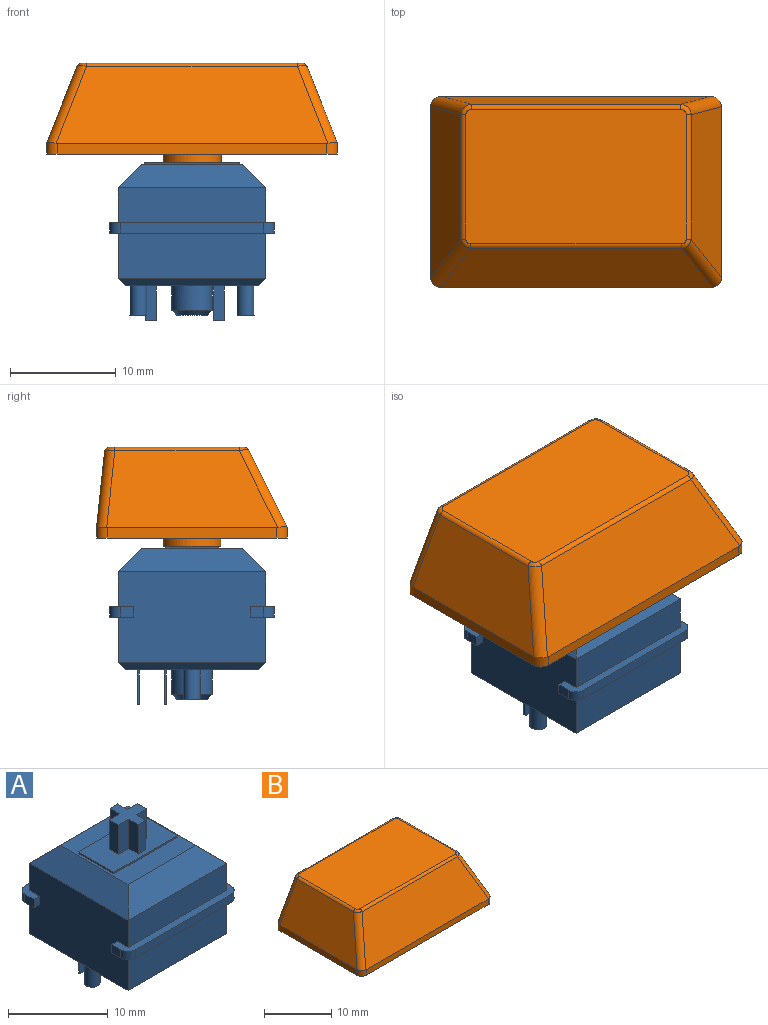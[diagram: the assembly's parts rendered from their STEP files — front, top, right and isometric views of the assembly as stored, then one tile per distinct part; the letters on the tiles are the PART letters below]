
ASSEMBLY  parts=2 mates=1
PART A: 69 faces, bbox 15.6x15.6x18.6 mm
  f0: plane 15.6x2.3mm, normal (0,0,-1), area 14.4mm2, adj f2,f3,f28,f30,f35,f60,f62,f63
  f1: plane 15.6x2.3mm, normal (0,0,-1), area 14.4mm2, adj f28,f30,f33,f34,f36,f59,f61,f64
  f2: plane 1.3x1mm, normal (1,0,0), area 1.3mm2, adj f0,f32,f62,f66
  f3: plane 1.3x1mm, normal (-1,0,0), area 1.3mm2, adj f0,f32,f63,f68
  f4: plane 15.6x2.3mm, normal (0,0,1), area 14.4mm2, adj f28,f30,f31,f33,f34,f36,f61,f64
  f5: plane 14x2.2mm, normal (-0.71,0,0.71), area 36.7mm2, adj f6,f7,f26,f30
  f6: plane 14x2.2mm, normal (0,-0.71,0.71), area 36.7mm2, adj f5,f7,f27,f31
  f7: plane 9.6x9.6mm, normal (0,0,1), area 47.2mm2, adj f5,f6,f8,f9,f10,f11,f26,f27
  f8: plane 5x0.2mm, normal (1,0,0), area 1mm2, adj f7,f9,f11,f12
  f9: plane 9x0.2mm, normal (0,1,0), area 1.8mm2, adj f7,f8,f10,f12
  f10: plane 5x0.2mm, normal (-1,0,0), area 1mm2, adj f7,f9,f11,f12
  f11: plane 9x0.2mm, normal (0,-1,0), area 1.8mm2, adj f7,f8,f10,f12
  f12: plane 9x5mm, normal (0,0,1), area 36.9mm2, adj f8,f9,f10,f11,f13,f14,f15,f16
  f13: plane 3.6x1.35mm, normal (1,0,0), area 4.9mm2, adj f12,f14,f24,f25
  f14: plane 3.6x1.08mm, normal (0,1,0), area 3.9mm2, adj f12,f13,f15,f25
  f15: plane 3.6x1.35mm, normal (-1,0,0), area 4.9mm2, adj f12,f14,f16,f25
  f16: plane 3.6x1.46mm, normal (0,1,0), area 5.3mm2, adj f12,f15,f17,f25
  f17: plane 3.6x1.3mm, normal (-1,0,0), area 4.7mm2, adj f12,f16,f18,f25
  f18: plane 3.6x1.46mm, normal (0,-1,0), area 5.3mm2, adj f12,f17,f19,f25
  f19: plane 3.6x1.35mm, normal (-1,0,0), area 4.9mm2, adj f12,f18,f20,f25
  f20: plane 3.6x1.08mm, normal (0,-1,0), area 3.9mm2, adj f12,f19,f21,f25
  f21: plane 3.6x1.35mm, normal (1,0,0), area 4.9mm2, adj f12,f20,f22,f25
  f22: plane 3.6x1.46mm, normal (0,-1,0), area 5.3mm2, adj f12,f21,f23,f25
  f23: plane 3.6x1.3mm, normal (1,0,0), area 4.7mm2, adj f12,f22,f24,f25
  f24: plane 3.6x1.46mm, normal (0,1,0), area 5.3mm2, adj f12,f13,f23,f25
  f25: plane 4x4mm, normal (0,0,1), area 8.1mm2, adj f13,f14,f15,f16,f17,f18,f19,f20
  f26: plane 14x2.2mm, normal (0,0.71,0.71), area 36.7mm2, adj f5,f7,f27,f29
  f27: plane 14x2.2mm, normal (0.71,0,0.71), area 36.7mm2, adj f6,f7,f26,f28
  f28: plane 14x8.6mm, normal (1,0,0), area 117.4mm2, adj f0,f1,f4,f27,f29,f31,f32,f55
  f29: plane 14x3.3mm, normal (0,1,0), area 46.2mm2, adj f26,f28,f30,f32
  f30: plane 14x8.6mm, normal (-1,0,0), area 117.4mm2, adj f0,f1,f4,f5,f29,f31,f32,f57
  f31: plane 14x3.3mm, normal (0,-1,0), area 46.2mm2, adj f4,f6,f28,f30
  f32: plane 15.6x2.3mm, normal (0,0,1), area 14.4mm2, adj f2,f3,f28,f29,f30,f35,f62,f63
  f33: plane 13.6x1mm, normal (0,-1,0), area 13.6mm2, adj f1,f4,f61,f64
  f34: plane 1.3x1mm, normal (1,0,0), area 1.3mm2, adj f1,f4,f61,f65
  f35: plane 13.6x1mm, normal (0,1,0), area 13.6mm2, adj f0,f32,f62,f63
  f36: plane 1.3x1mm, normal (-1,0,0), area 1.3mm2, adj f1,f4,f64,f67
  f37: plane 2.85x2.85mm, normal (0,0,-1), area 6.4mm2, adj f38
  f38: cone r=1.43mm half-angle=45deg, axis (0,0,1), area 7.4mm2, adj f37,f43
  f39: plane 1x0.2mm, normal (0,0,-1), area 0.2mm2, adj f44,f45,f46,f47
  f40: plane 1x0.2mm, normal (0,0,-1), area 0.2mm2, adj f48,f49,f50,f51
  f41: plane 1.6x1.6mm, normal (0,0,-1), area 2mm2, adj f52
  f42: plane 1.6x1.6mm, normal (0,0,-1), area 2mm2, adj f53
  f43: cylinder r=1.93mm len=3.85mm, axis (0,0,1), area 27.8mm2, adj f38,f54
  f44: plane 3.3x0.2mm, normal (-1,0,0), area 0.7mm2, adj f39,f45,f47,f54
  f45: plane 3.3x1mm, normal (0,1,0), area 3.3mm2, adj f39,f44,f46,f54
  f46: plane 3.3x0.2mm, normal (1,0,0), area 0.7mm2, adj f39,f45,f47,f54
  f47: plane 3.3x1mm, normal (0,-1,0), area 3.3mm2, adj f39,f44,f46,f54
  f48: plane 3.3x0.2mm, normal (-1,0,0), area 0.7mm2, adj f40,f49,f51,f54
  f49: plane 3.3x1mm, normal (0,1,0), area 3.3mm2, adj f40,f48,f50,f54
  f50: plane 3.3x0.2mm, normal (1,0,0), area 0.7mm2, adj f40,f49,f51,f54
  f51: plane 3.3x1mm, normal (0,-1,0), area 3.3mm2, adj f40,f48,f50,f54
  f52: cylinder r=0.8mm len=2.8mm, axis (0,0,1), area 14.1mm2, adj f41,f54
  f53: cylinder r=0.8mm len=2.8mm, axis (0,0,1), area 14.1mm2, adj f42,f54
  f54: plane 12.6x12.6mm, normal (0,0,-1), area 142.7mm2, adj f43,f44,f45,f46,f47,f48,f49,f50
  f55: plane 14x0.7mm, normal (0.71,0,-0.71), area 13.2mm2, adj f28,f54,f56,f58
  f56: plane 14x0.7mm, normal (0,0.71,-0.71), area 13.2mm2, adj f54,f55,f57,f60
  f57: plane 14x0.7mm, normal (-0.71,0,-0.71), area 13.2mm2, adj f30,f54,f56,f58
  f58: plane 14x0.7mm, normal (0,-0.71,-0.71), area 13.2mm2, adj f54,f55,f57,f59
  f59: plane 14x4.3mm, normal (0,-1,0), area 60.2mm2, adj f1,f28,f30,f58
  f60: plane 14x4.3mm, normal (0,1,0), area 60.2mm2, adj f0,f28,f30,f56
  f61: cylinder r=1mm len=1mm, axis (0,0,-1), area 1.6mm2, adj f1,f4,f33,f34
  f62: cylinder r=1mm len=1mm, axis (0,0,1), area 1.6mm2, adj f0,f2,f32,f35
  f63: cylinder r=1mm len=1mm, axis (0,0,-1), area 1.6mm2, adj f0,f3,f32,f35
  f64: cylinder r=1mm len=1mm, axis (0,0,1), area 1.6mm2, adj f1,f4,f33,f36
  f65: plane 1x0.8mm, normal (0,1,0), area 0.8mm2, adj f1,f4,f28,f34
  f66: plane 1x0.8mm, normal (0,-1,0), area 0.8mm2, adj f0,f2,f28,f32
  f67: plane 1x0.8mm, normal (0,1,0), area 0.8mm2, adj f1,f4,f30,f36
  f68: plane 1x0.8mm, normal (0,-1,0), area 0.8mm2, adj f0,f3,f30,f32
PART B: 50 faces, bbox 27.7x18.1x9.4 mm
  f0: plane 16.1x1mm, normal (-1,0,0), area 16.1mm2, adj f4,f6,f14,f16
  f1: plane 25.58x1mm, normal (0,-1,0), area 25.6mm2, adj f4,f7,f12,f14
  f2: plane 16.1x1mm, normal (1,0,0), area 16.1mm2, adj f4,f8,f10,f12
  f3: plane 25.58x1mm, normal (0,1,0), area 25.6mm2, adj f4,f9,f10,f11,f16,f17
  f4: plane 27.58x18.1mm, normal (0,0,-1), area 86.5mm2, adj f0,f1,f2,f3,f10,f12,f14,f16
  f5: plane 20.89x12.74mm, normal (0,0,1), area 266mm2, adj f18,f19,f20,f21,f22,f23,f24,f25
  f6: plane 16.2x7.29mm, normal (-0.93,0,0.37), area 109.6mm2, adj f0,f14,f15,f16,f17,f20
  f7: plane 25.78x7.33mm, normal (0,-0.89,0.45), area 187.4mm2, adj f1,f12,f13,f14,f15,f19
  f8: plane 16.2x7.29mm, normal (0.93,0,0.37), area 109.6mm2, adj f2,f10,f11,f12,f13,f23
  f9: plane 25.51x7.15mm, normal (0,0.99,0.1), area 163.1mm2, adj f3,f11,f17,f24
  f10: cylinder r=1mm len=1.02mm, axis (0,0,1), area 1.6mm2, adj f2,f3,f4,f8,f11
  f11: cylinder r=1mm len=7.69mm, axis (-0.37,-0.1,0.93), area 12mm2, adj f3,f8,f9,f10,f25
  f12: cylinder r=1mm len=1.07mm, axis (0,0,-1), area 1.6mm2, adj f1,f2,f4,f7,f8,f13
  f13: cylinder r=1mm len=7.55mm, axis (0.33,-0.42,-0.84), area 12.2mm2, adj f7,f8,f12,f21
  f14: cylinder r=1mm len=1.07mm, axis (0,0,1), area 1.6mm2, adj f0,f1,f4,f6,f7,f15
  f15: cylinder r=1mm len=7.55mm, axis (0.33,0.42,0.84), area 12.2mm2, adj f6,f7,f14,f18
  f16: cylinder r=1mm len=1.02mm, axis (0,0,-1), area 1.6mm2, adj f0,f3,f4,f6,f17
  f17: cylinder r=1mm len=7.69mm, axis (-0.37,0.1,-0.93), area 12mm2, adj f3,f6,f9,f16,f22
  f18: bspline ~1.06x1.03mm, area 0.6mm2, adj f5,f15,f19,f20
  f19: cylinder r=0.5mm len=20mm, axis (1,0,0), area 11.1mm2, adj f5,f7,f18,f21
  f20: cylinder r=0.5mm len=11.79mm, axis (0,-1,0), area 7mm2, adj f5,f6,f18,f22
  f21: bspline ~0.92x0.92mm, area 0.6mm2, adj f5,f13,f19,f23
  f22: bspline ~0.99x0.99mm, area 0.8mm2, adj f5,f17,f20,f24
  f23: cylinder r=0.5mm len=11.79mm, axis (0,-1,0), area 7mm2, adj f5,f8,f21,f25
  f24: cylinder r=0.5mm len=19.86mm, axis (1,0,0), area 14.6mm2, adj f5,f9,f22,f25
  f25: bspline ~0.99x0.98mm, area 0.8mm2, adj f5,f11,f23,f24
  f26: plane 16.1x0.81mm, normal (1,0,0), area 13mm2, adj f4,f27,f29,f31,f32
  f27: plane 25.58x0.76mm, normal (0,1,0), area 19.5mm2, adj f4,f26,f28,f32
  f28: plane 16.1x0.81mm, normal (-1,0,0), area 13mm2, adj f4,f27,f29,f32,f33
  f29: plane 25.58x0.95mm, normal (0,-1,0), area 24.2mm2, adj f4,f26,f28,f31,f33,f34
  f30: plane 20.21x11.98mm, normal (0,0,-1), area 218.4mm2, adj f31,f32,f33,f34,f45
  f31: plane 16.08x6.79mm, normal (0.93,0,-0.37), area 102.5mm2, adj f26,f29,f30,f32,f34
  f32: plane 25.58x6.84mm, normal (0,0.89,-0.45), area 175.1mm2, adj f26,f27,f28,f30,f31,f33
  f33: plane 16.08x6.79mm, normal (-0.93,0,-0.37), area 102.5mm2, adj f28,f29,f30,f32,f34
  f34: plane 25.47x6.65mm, normal (0,-0.99,-0.1), area 152.8mm2, adj f29,f30,f31,f33
  f35: plane 8.4x1.35mm, normal (-1,0,0), area 11.3mm2, adj f36,f44,f47,f49
  f36: plane 8.4x1.5mm, normal (0,-1,0), area 12.6mm2, adj f35,f37,f44,f49
  f37: plane 8.4x1.3mm, normal (-1,0,0), area 10.9mm2, adj f36,f38,f44,f49
  f38: plane 8.4x1.5mm, normal (0,1,0), area 12.6mm2, adj f37,f39,f44,f49
  f39: plane 8.4x1.35mm, normal (-1,0,0), area 11.3mm2, adj f38,f40,f44,f49
  f40: plane 8.4x1mm, normal (0,1,0), area 8.4mm2, adj f39,f41,f44,f49
  f41: plane 8.4x1.35mm, normal (1,0,0), area 11.3mm2, adj f40,f42,f44,f49
  f42: plane 8.4x1.5mm, normal (0,1,0), area 12.6mm2, adj f41,f43,f44,f49
  f43: plane 8.4x1.3mm, normal (1,0,0), area 10.9mm2, adj f42,f44,f46,f49
  f44: plane 5.5x5.5mm, normal (0,0,-1), area 15.9mm2, adj f35,f36,f37,f38,f39,f40,f41,f42
  f45: cylinder r=2.75mm len=8.4mm, axis (0,0,-1), area 145.1mm2, adj f30,f44
  f46: plane 8.4x1.5mm, normal (0,-1,0), area 12.6mm2, adj f43,f44,f48,f49
  f47: plane 8.4x1mm, normal (0,-1,0), area 8.4mm2, adj f35,f44,f48,f49
  f48: plane 8.4x1.35mm, normal (1,0,0), area 11.3mm2, adj f44,f46,f47,f49
  f49: plane 4x4mm, normal (0,0,-1), area 7.9mm2, adj f35,f36,f37,f38,f39,f40,f41,f42
PLACE A at identity fixed
PLACE B t=(0,0,11.7)mm
MATE fastened B.f45 <-> A.f38  axis (0,0,-1) through (0,0,11.7)mm
